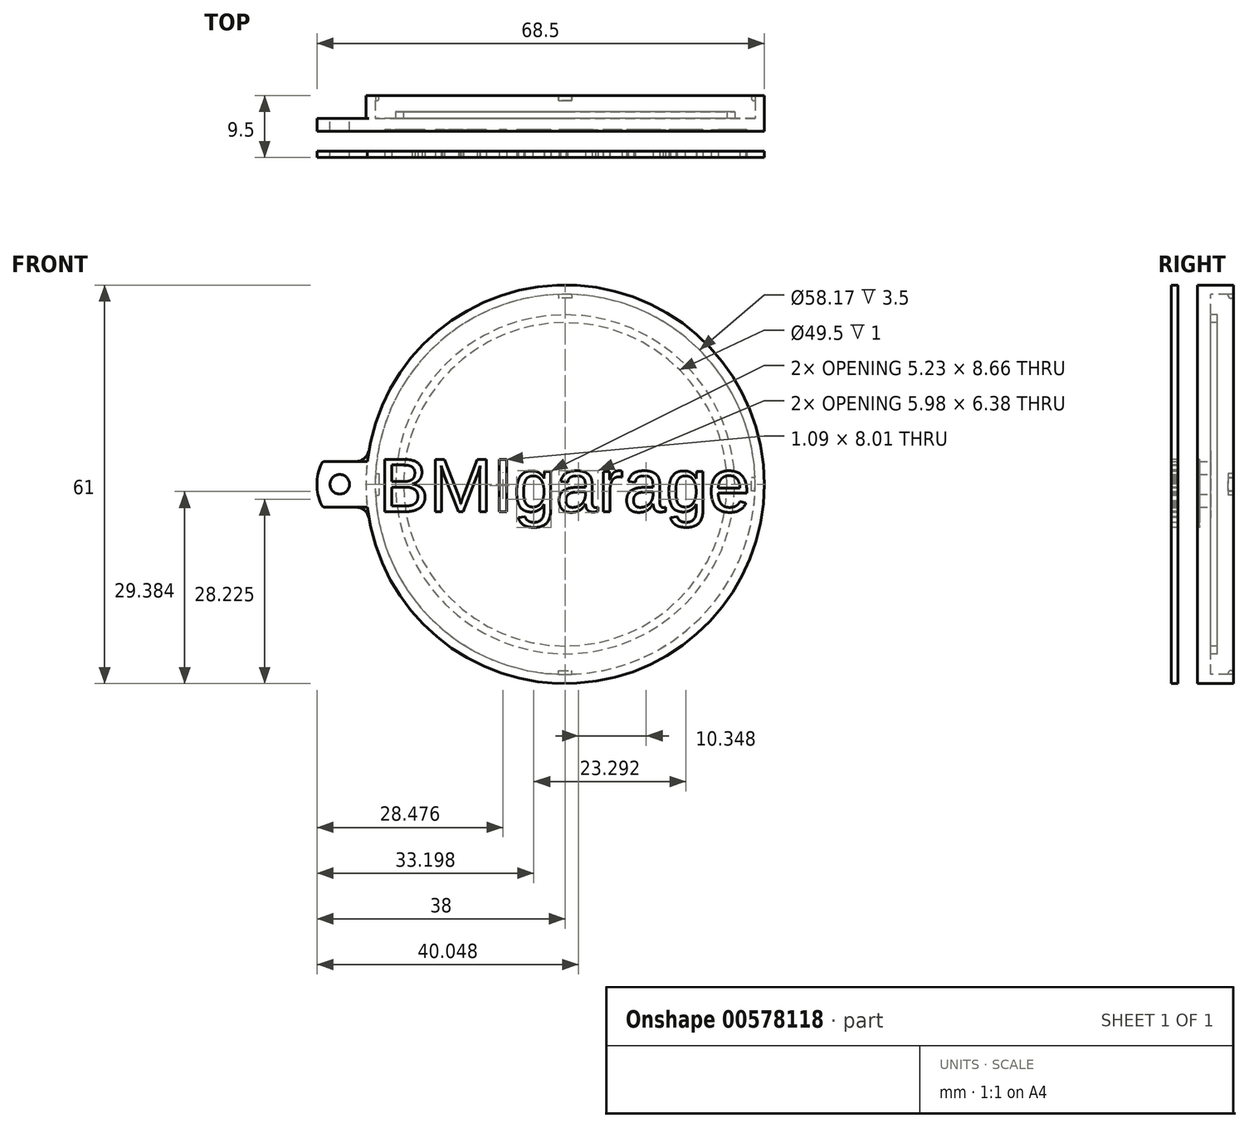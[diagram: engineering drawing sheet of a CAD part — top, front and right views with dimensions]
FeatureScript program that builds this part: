
annotation { "Feature Type Name" : "Feature", "Feature Type Description" : "" }
export const myFeature = defineFeature(function(context is Context, id is Id, definition is map)
    precondition{}
    {
        {
            var Q0;
            Q0=qCreatedBy(makeId("Front.planeOp"),FACE);
            var sketch = newSketch(context, id + "F0", { "sketchPlane" : qUnion([Q0])});
            skCircle(sketch, "E0", {"center": v(0, 0) * mm, "radius": 30.5 * mm});
            skCircle(sketch, "E1", {"center": v(0, 0) * mm, "radius": 25.95 * mm});
            skCircle(sketch, "E2", {"center": v(0, 0) * mm, "radius": 24.75 * mm});
            skCircle(sketch, "E3", {"center": v(0, 0) * mm, "radius": 29.08 * mm});
            skLineSegment(sketch, "E4.bottom", {"start": v(-29.04, -1.64) * mm, "end": v(-28.48, -1.64) * mm});
            skLineSegment(sketch, "E4.top", {"start": v(-29.04, 1.64) * mm, "end": v(-28.48, 1.64) * mm});
            skLineSegment(sketch, "E5.left", {"start": v(-1, -29.07) * mm, "end": v(-1, -28.51) * mm});
            skLineSegment(sketch, "E5.right", {"start": v(1, -29.07) * mm, "end": v(1, -28.51) * mm});
            skPoint(sketch, "E6.orphan", {"position": v(-31.55, -1.64) * mm});
            skPoint(sketch, "E7.orphan", {"position": v(-31.55, 1.64) * mm});
            skPoint(sketch, "E8.orphan", {"position": v(31.55, -1.64) * mm});
            skPoint(sketch, "E9.orphan", {"position": v(31.55, 1.64) * mm});
            skLineSegment(sketch, "E10.trimOffspring", {"start": v(28.51, 1) * mm, "end": v(29.07, 1) * mm});
            skLineSegment(sketch, "E11.trimOffspring", {"start": v(28.51, -1) * mm, "end": v(29.07, -1) * mm});
            skPoint(sketch, "E12.orphan", {"position": v(-1, 47.63) * mm});
            skPoint(sketch, "E13.orphan", {"position": v(1, 47.63) * mm});
            skLineSegment(sketch, "E14.trimOffspring", {"start": v(-1, 28.47) * mm, "end": v(-1, 29.07) * mm});
            skLineSegment(sketch, "E15.trimOffspring", {"start": v(1, 28.51) * mm, "end": v(1, 29.07) * mm});
            skPoint(sketch, "E16.orphan", {"position": v(-1, -47.63) * mm});
            skPoint(sketch, "E17.orphan", {"position": v(1, -47.63) * mm});
            skLineSegment(sketch, "E18", {"start": v(-1, 28.47) * mm, "end": v(1, 28.51) * mm});
            skPoint(sketch, "E19.trimOffspring.end.orphan", {"position": v(-1, 27.87) * mm});
            skPoint(sketch, "E20.orphan", {"position": v(1, 27.95) * mm});
            skLineSegment(sketch, "E21", {"start": v(28.51, -1) * mm, "end": v(28.51, 1) * mm});
            skLineSegment(sketch, "E22", {"start": v(-1, -28.51) * mm, "end": v(1, -28.51) * mm});
            skLineSegment(sketch, "E23", {"start": v(-28.48, 1.64) * mm, "end": v(-28.48, -1.64) * mm});
            skPoint(sketch, "E24.orphan", {"position": v(-27.93, 1.64) * mm});
            skPoint(sketch, "E25.orphan", {"position": v(-27.93, -1.64) * mm});
            skPoint(sketch, "E26.orphan", {"position": v(27.95, 1) * mm});
            skPoint(sketch, "E27.orphan", {"position": v(27.95, -1) * mm});
            skPoint(sketch, "E28.trimOffspring.start.orphan", {"position": v(-1, -27.95) * mm});
            skPoint(sketch, "E29.orphan", {"position": v(1, -27.95) * mm});
            skCircle(sketch, "E30", {"center": v(-34.5, 0) * mm, "radius": 1.5 * mm});
            skPoint(sketch, "E30.centerSnap0", {"position": v(-28.48, 0) * mm});
            skLineSegment(sketch, "E31", {"start": v(-30.3, 3.5) * mm, "end": v(-36.76, 3.5) * mm});
            skLineSegment(sketch, "E32.MirrorCS", {"start": v(-30.3, -3.5) * mm, "end": v(-36.76, -3.5) * mm});
            skArc(sketch, "E33.trimOffspring", {"start": v(-37.3, 3.16) * mm, "mid": v(-38, 0) * mm, "end": v(-37.3, -3.16) * mm});
            skPoint(sketch, "E34.visualSharp", {"position": v(-37.13, 3.5) * mm});
            skArc(sketch, "E34.filletArc", {"start": v(-36.76, 3.5) * mm, "mid": v(-37.08, 3.4) * mm, "end": v(-37.3, 3.16) * mm});
            skPoint(sketch, "E35.visualSharp", {"position": v(-37.13, -3.5) * mm});
            skArc(sketch, "E35.filletArc", {"start": v(-37.3, -3.16) * mm, "mid": v(-37.08, -3.4) * mm, "end": v(-36.76, -3.5) * mm});
            skSolve(sketch);
        }
        {
            var Q0;
            Q0=makeQuery(id+"F0.imprint","IMPRINT",FACE,{"disambiguationData":[TD([[makeQuery(id+"F0.imprint","IMPRINT",EDGE,{"derivedFrom":sQuery(id+"F0.wireOp",EDGE,"E2")}),1.0]])]});
            var Q1;
            Q1=makeQuery(id+"F0.imprint","IMPRINT",FACE,{"disambiguationData":[TD([[makeQuery(id+"F0.imprint","IMPRINT",EDGE,{"derivedFrom":sQuery(id+"F0.wireOp",EDGE,"E1")}),1.0]])]});
            var Q2;
            Q2=makeQuery(id+"F0.imprint","IMPRINT",FACE,{"disambiguationData":[TD([[makeQuery(id+"F0.imprint","IMPRINT",EDGE,{"derivedFrom":sQuery(id+"F0.wireOp",EDGE,"fVDYAqdK-oLy6-3NBf-5w80-oD4vA6zZdJef")}),1.0]])]});
            var Q3;
            Q3=makeQuery(id+"F0.imprint","IMPRINT",FACE,{"disambiguationData":[TD([[makeQuery(id+"F0.imprint","IMPRINT",EDGE,{"derivedFrom":sQuery(id+"F0.wireOp",EDGE,"fVDYAqdK-oLy6-3NBf-5w80-oD4vA6zZdJef")}),-1.0]])]});
            var Q4;
            Q4=makeQuery(id+"F0.imprint","IMPRINT",FACE,{"disambiguationData":[TD([[makeQuery(id+"F0.imprint","IMPRINT",EDGE,{"derivedFrom":sQuery(id+"F0.wireOp",EDGE,"E0")}),1.0]])]});
            var Q5;
            {var subQ0=sQuery(id+"F0.wireOp",EDGE,"E5.left");Q5=makeQuery(id+"F0.imprint","IMPRINT",FACE,{"disambiguationData":[TD([[makeQuery(id+"F0.imprint","IMPRINT",EDGE,{"derivedFrom":subQ0}),-1.0]])]});}
            var Q6;
            Q6=makeQuery(id+"F0.imprint","IMPRINT",FACE,{"disambiguationData":[TD([[makeQuery(id+"F0.imprint","IMPRINT",EDGE,{"derivedFrom":sQuery(id+"F0.wireOp",EDGE,"E19.trimOffspring")}),-1.0]])]});
            var Q7;
            Q7=makeQuery(id+"F0.imprint","IMPRINT",FACE,{"disambiguationData":[TD([[makeQuery(id+"F0.imprint","IMPRINT",EDGE,{"derivedFrom":sQuery(id+"F0.wireOp",EDGE,"E1")}),-1.0]])]});
            var Q8;
            {var subQ0=sQuery(id+"F0.wireOp",EDGE,"E10.trimOffspring");Q8=makeQuery(id+"F0.imprint","IMPRINT",FACE,{"disambiguationData":[TD([[makeQuery(id+"F0.imprint","IMPRINT",EDGE,{"derivedFrom":subQ0}),-1.0]])]});}
            var Q9;
            {var subQ0=sQuery(id+"F0.wireOp",EDGE,"E14.trimOffspring");Q9=makeQuery(id+"F0.imprint","IMPRINT",FACE,{"disambiguationData":[TD([[makeQuery(id+"F0.imprint","IMPRINT",EDGE,{"derivedFrom":subQ0}),-1.0]])]});}
            var Q10;
            {var subQ0=sQuery(id+"F0.wireOp",EDGE,"E4.bottom");Q10=makeQuery(id+"F0.imprint","IMPRINT",FACE,{"disambiguationData":[TD([[makeQuery(id+"F0.imprint","IMPRINT",EDGE,{"derivedFrom":subQ0}),1.0]])]});}
            var Q11;
            Q11=makeQuery(id+"F0.imprint","IMPRINT",FACE,{"disambiguationData":[TD([[makeQuery(id+"F0.imprint","IMPRINT",EDGE,{"derivedFrom":sQuery(id+"F0.wireOp",EDGE,"E30")}),-1.0]])]});
            extrude(context, id + "F1", {"entities" : qUnion([Q0, Q1, Q2, Q3, Q4, Q5, Q6, Q7, Q8, Q9, Q10, Q11]), "depth" : 2 * mm, "offsetDistance" : 25 * mm});
        }
        {
            var Q0;
            Q0=makeQuery(id+"F0.imprint","IMPRINT",FACE,{"disambiguationData":[TD([[makeQuery(id+"F0.imprint","IMPRINT",EDGE,{"derivedFrom":sQuery(id+"F0.wireOp",EDGE,"E1")}),1.0]])]});
            extrude(context, id + "F2", {"entities" : qUnion([Q0]), "operationType" : NewBodyOperationType.ADD, "oppositeDirection" : true, "depth" : 1 * mm, "offsetDistance" : 25 * mm});
        }
        {
            var Q0;
            Q0=makeQuery(id+"F0.imprint","IMPRINT",FACE,{"disambiguationData":[TD([[makeQuery(id+"F0.imprint","IMPRINT",EDGE,{"derivedFrom":sQuery(id+"F0.wireOp",EDGE,"E0")}),1.0]])]});
            extrude(context, id + "F3", {"entities" : qUnion([Q0]), "operationType" : NewBodyOperationType.ADD, "oppositeDirection" : true, "depth" : 3.5 * mm, "offsetDistance" : 25 * mm});
        }
        {
            var Q0;
            {var subQ0=sQuery(id+"F0.wireOp",EDGE,"E5.left");Q0=makeQuery(id+"F0.imprint","IMPRINT",FACE,{"disambiguationData":[TD([[makeQuery(id+"F0.imprint","IMPRINT",EDGE,{"derivedFrom":subQ0}),-1.0]])]});}
            var Q1;
            {var subQ0=sQuery(id+"F0.wireOp",EDGE,"E10.trimOffspring");Q1=makeQuery(id+"F0.imprint","IMPRINT",FACE,{"disambiguationData":[TD([[makeQuery(id+"F0.imprint","IMPRINT",EDGE,{"derivedFrom":subQ0}),-1.0]])]});}
            var Q2;
            {var subQ0=sQuery(id+"F0.wireOp",EDGE,"E4.bottom");Q2=makeQuery(id+"F0.imprint","IMPRINT",FACE,{"disambiguationData":[TD([[makeQuery(id+"F0.imprint","IMPRINT",EDGE,{"derivedFrom":subQ0}),1.0]])]});}
            var Q3;
            {var subQ0=sQuery(id+"F0.wireOp",EDGE,"E14.trimOffspring");Q3=makeQuery(id+"F0.imprint","IMPRINT",FACE,{"disambiguationData":[TD([[makeQuery(id+"F0.imprint","IMPRINT",EDGE,{"derivedFrom":subQ0}),-1.0]])]});}
            extrude(context, id + "F4", {"entities" : qUnion([Q0, Q1, Q2, Q3]), "operationType" : NewBodyOperationType.ADD, "oppositeDirection" : true, "depth" : 3.5 * mm, "offsetDistance" : 25 * mm, "hasSecondDirection" : true, "secondDirectionOppositeDirection" : true, "secondDirectionDepth" : 2.7 * mm});
        }
        {
            var Q0;
            Q0=makeQuery(id+"F4.opExtrude","CAP_EDGE",EDGE,{"disambiguationData":[OSD([sQuery(id+"F0.wireOp",EDGE,"E18")])],"isStart":false});
            var Q1;
            Q1=makeQuery(id+"F4.opExtrude","CAP_EDGE",EDGE,{"disambiguationData":[OSD([sQuery(id+"F0.wireOp",EDGE,"E18")])],"isStart":true});
            var Q2;
            Q2=makeQuery(id+"F4.opExtrude","CAP_EDGE",EDGE,{"disambiguationData":[OSD([sQuery(id+"F0.wireOp",EDGE,"E23")])],"isStart":false});
            var Q3;
            Q3=makeQuery(id+"F4.opExtrude","CAP_EDGE",EDGE,{"disambiguationData":[OSD([sQuery(id+"F0.wireOp",EDGE,"E23")])],"isStart":true});
            var Q4;
            Q4=makeQuery(id+"F4.opExtrude","CAP_EDGE",EDGE,{"disambiguationData":[OSD([sQuery(id+"F0.wireOp",EDGE,"E22")])],"isStart":false});
            var Q5;
            Q5=makeQuery(id+"F4.opExtrude","CAP_EDGE",EDGE,{"disambiguationData":[OSD([sQuery(id+"F0.wireOp",EDGE,"E22")])],"isStart":true});
            var Q6;
            Q6=makeQuery(id+"F4.opExtrude","CAP_EDGE",EDGE,{"disambiguationData":[OSD([sQuery(id+"F0.wireOp",EDGE,"E21")])],"isStart":false});
            var Q7;
            Q7=makeQuery(id+"F4.opExtrude","CAP_EDGE",EDGE,{"disambiguationData":[OSD([sQuery(id+"F0.wireOp",EDGE,"E21")])],"isStart":true});
            fillet(context, id + "F5", {"entities" : qUnion([Q0, Q1, Q2, Q3, Q4, Q5, Q6, Q7]), "radius" : 0.4 * mm, "tangentPropagation" : true, "allowEdgeOverflow" : false});
        }
        {
            var Q0;
            Q0=makeQuery(id+"F1.opExtrude","CAP_FACE",FACE,{"disambiguationData":[OSD([sQuery(id+"F0.wireOp",EDGE,"E0")])],"isStart":false});
            var sketch = newSketch(context, id + "F6", { "sketchPlane" : qUnion([Q0])});
            skText(sketch, "E36", { "text": "BMIgarage", "fontName": "Arimo-Regular.ttf"});
            skLineSegment(sketch, "E37", {"start": v(-28.6, 0) * mm, "end": v(28.6, 0) * mm, "construction": true});
            skPoint(sketch, "E38", {"position": v(0, 0) * mm});
            const initialGuessF6  = {"E36": [-0.0286, -0.00419, 1, 0, 0.00838]};
            skSetInitialGuess(sketch, initialGuessF6);
            skSolve(sketch);
        }
        {
            var Q0;
            Q0=makeQuery(id+"F0.imprint","IMPRINT",FACE,{"disambiguationData":[TD([[makeQuery(id+"F0.imprint","IMPRINT",EDGE,{"derivedFrom":sQuery(id+"F0.wireOp",EDGE,"E2")}),1.0]])]});
            var Q1;
            Q1=makeQuery(id+"F0.imprint","IMPRINT",FACE,{"disambiguationData":[TD([[makeQuery(id+"F0.imprint","IMPRINT",EDGE,{"derivedFrom":sQuery(id+"F0.wireOp",EDGE,"E1")}),-1.0]])]});
            var Q2;
            {var subQ3=sQuery(id+"F0.wireOp",EDGE,"E0");var subQ4=makeQuery(id+"F0.imprint","INTERSECT",VERTEX,{"derivedFrom":[subQ3,sQuery(id+"F0.wireOp",EDGE,"E31")]});Q2=makeQuery(id+"F0.imprint","IMPRINT",FACE,{"disambiguationData":[TD([[makeQuery(id+"F0.imprint","IMPRINT",EDGE,{"disambiguationData":[TD([[subQ4,-1.0]])],"derivedFrom":subQ3}),1.0]])]});}
            var Q3;
            Q3=makeQuery(id+"F0.imprint","IMPRINT",FACE,{"disambiguationData":[TD([[makeQuery(id+"F0.imprint","IMPRINT",EDGE,{"derivedFrom":sQuery(id+"F0.wireOp",EDGE,"E1")}),1.0]])]});
            var Q4;
            {var subQ0=sQuery(id+"F0.wireOp",EDGE,"E14.trimOffspring");Q4=makeQuery(id+"F0.imprint","IMPRINT",FACE,{"disambiguationData":[TD([[makeQuery(id+"F0.imprint","IMPRINT",EDGE,{"derivedFrom":subQ0}),-1.0]])]});}
            var Q5;
            {var subQ0=sQuery(id+"F0.wireOp",EDGE,"E10.trimOffspring");Q5=makeQuery(id+"F0.imprint","IMPRINT",FACE,{"disambiguationData":[TD([[makeQuery(id+"F0.imprint","IMPRINT",EDGE,{"derivedFrom":subQ0}),-1.0]])]});}
            var Q6;
            {var subQ0=sQuery(id+"F0.wireOp",EDGE,"E5.left");Q6=makeQuery(id+"F0.imprint","IMPRINT",FACE,{"disambiguationData":[TD([[makeQuery(id+"F0.imprint","IMPRINT",EDGE,{"derivedFrom":subQ0}),-1.0]])]});}
            var Q7;
            Q7=makeQuery(id+"F0.imprint","IMPRINT",FACE,{"disambiguationData":[TD([[makeQuery(id+"F0.imprint","IMPRINT",EDGE,{"derivedFrom":sQuery(id+"F0.wireOp",EDGE,"E30")}),-1.0]])]});
            var Q8;
            {var subQ0=sQuery(id+"F0.wireOp",EDGE,"E4.bottom");Q8=makeQuery(id+"F0.imprint","IMPRINT",FACE,{"disambiguationData":[TD([[makeQuery(id+"F0.imprint","IMPRINT",EDGE,{"derivedFrom":subQ0}),1.0]])]});}
            extrude(context, id + "F7", {"entities" : qUnion([Q0, Q1, Q2, Q3, Q4, Q5, Q6, Q7, Q8]), "depth" : 6 * mm, "offsetDistance" : 25 * mm, "hasSecondDirection" : true, "secondDirectionOppositeDirection" : false, "secondDirectionDepth" : 5 * mm});
        }
        {
            var Q0;
            Q0 = qSketchRegion(id + "F6", true);
            extrude(context, id + "F8", {"entities" : qUnion([Q0]), "operationType" : NewBodyOperationType.REMOVE, "oppositeDirection" : true, "depth" : 0.3 * mm, "offsetDistance" : 25 * mm, "hasSecondDirection" : true, "secondDirectionOppositeDirection" : false, "secondDirectionDepth" : 25 * mm});
        }
        {
            var Q0;
            Q0=makeQuery(id+"F3.opExtrude","CAP_EDGE",EDGE,{"disambiguationData":[OSD([sQuery(id+"F0.wireOp",EDGE,"E0")])],"isStart":true});
            var Q1;
            Q1=makeQuery(id+"F1.opExtrude","SWEPT_EDGE",EDGE,{"disambiguationData":[OSD([sQuery(id+"F0.wireOp",EDGE,"E0"),sQuery(id+"F0.wireOp",EDGE,"E31")])]});
            var Q2;
            Q2=makeQuery(id+"F1.opExtrude","SWEPT_EDGE",EDGE,{"disambiguationData":[OSD([sQuery(id+"F0.wireOp",EDGE,"E0"),sQuery(id+"F0.wireOp",EDGE,"E32.MirrorCS")])]});
            fillet(context, id + "F9", {"entities" : qUnion([Q0, Q1, Q2]), "radius" : 2 * mm, "tangentPropagation" : true, "allowEdgeOverflow" : false});
        }
    });
